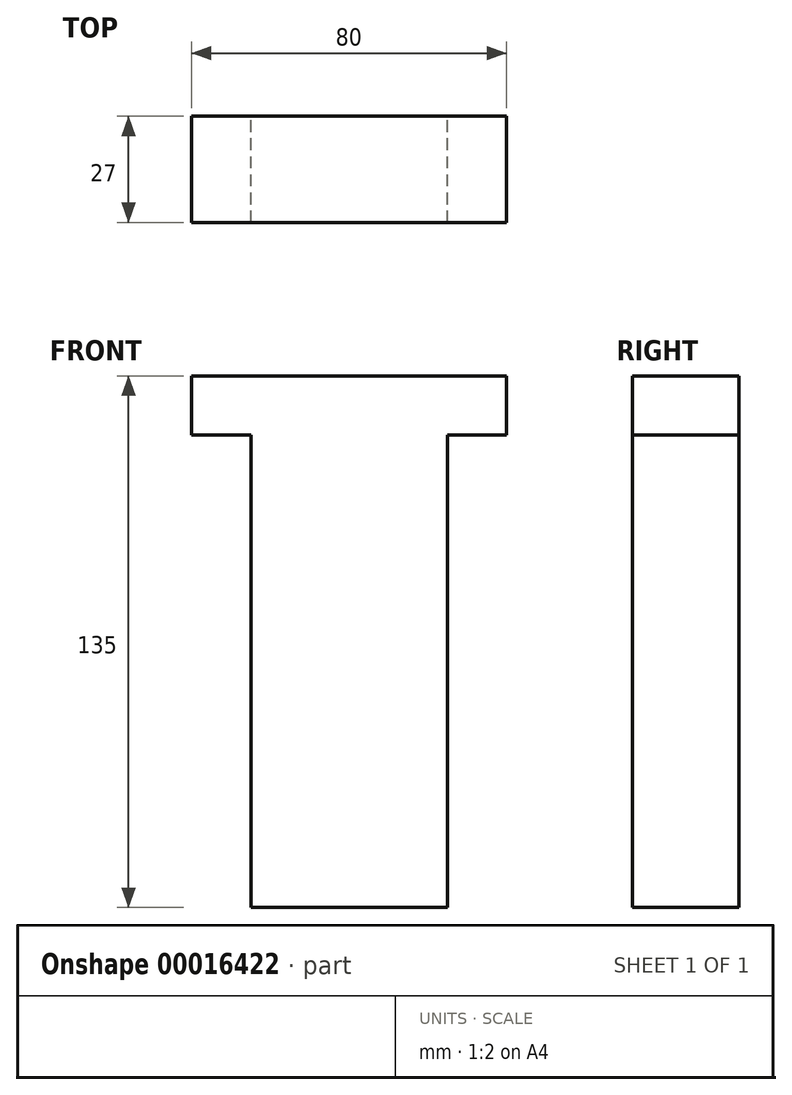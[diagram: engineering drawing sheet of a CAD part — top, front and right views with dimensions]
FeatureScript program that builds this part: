
annotation { "Feature Type Name" : "Feature", "Feature Type Description" : "" }
export const myFeature = defineFeature(function(context is Context, id is Id, definition is map)
    precondition{}
    {
        {
            var Q0;
            Q0=qCreatedBy(makeId("Front.planeOp"),FACE);
            var sketch = newSketch(context, id + "F0", { "sketchPlane" : qUnion([Q0])});
            skLineSegment(sketch, "E0", {"start": v(-40, 0) * mm, "end": v(-24.95, 0) * mm});
            skLineSegment(sketch, "E1", {"start": v(25.05, 0) * mm, "end": v(25.05, -120) * mm});
            skLineSegment(sketch, "E2", {"start": v(25.05, -120) * mm, "end": v(-24.95, -120) * mm});
            skLineSegment(sketch, "E3", {"start": v(-24.95, -120) * mm, "end": v(-24.95, 0) * mm});
            skLineSegment(sketch, "E4", {"start": v(0, 0) * mm, "end": v(0, 15) * mm});
            skLineSegment(sketch, "E5.0", {"start": v(40, 0) * mm, "end": v(40, 15) * mm});
            skLineSegment(sketch, "E6.0", {"start": v(-40, 0) * mm, "end": v(-40, 15) * mm});
            skLineSegment(sketch, "E7", {"start": v(-40, 15) * mm, "end": v(40, 15) * mm});
            skLineSegment(sketch, "E8.trimOffspring", {"start": v(25.05, 0) * mm, "end": v(40, 0) * mm});
            skSolve(sketch);
        }
        {
            var Q0;
            Q0=makeQuery(id+"F0.imprint","IMPRINT",FACE,{"disambiguationData":[TD([[makeQuery(id+"F0.imprint","IMPRINT",EDGE,{"derivedFrom":sQuery(id+"F0.wireOp",EDGE,"E0")}),1.0]])]});
            extrude(context, id + "F1", {"entities" : qUnion([Q0]), "depth" : 27 * mm});
        }
    });
